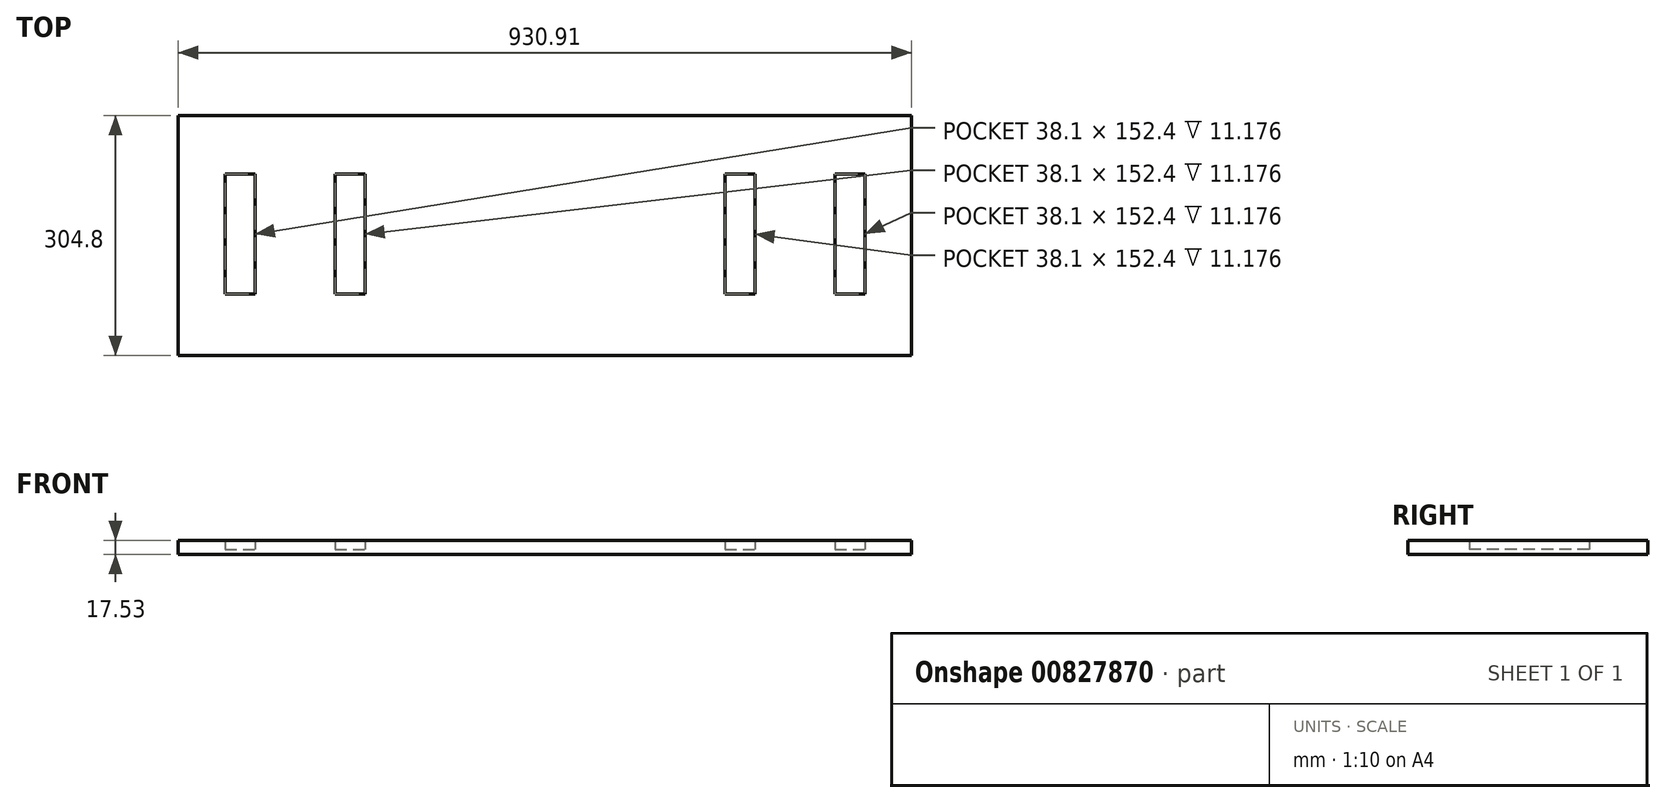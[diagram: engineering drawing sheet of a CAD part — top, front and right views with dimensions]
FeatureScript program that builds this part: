
annotation { "Feature Type Name" : "Feature", "Feature Type Description" : "" }
export const myFeature = defineFeature(function(context is Context, id is Id, definition is map)
    precondition{}
    {
        {
            var Q0;
            Q0=qCreatedBy(makeId("Top.planeOp"),FACE);
            var sketch = newSketch(context, id + "F0", { "sketchPlane" : qUnion([Q0])});
            skLineSegment(sketch, "E0.bottom", {"start": v(-457.2, 150.48) * mm, "end": v(457.2, 150.48) * mm});
            skLineSegment(sketch, "E0.top", {"start": v(-457.2, -154.32) * mm, "end": v(457.2, -154.32) * mm});
            skLineSegment(sketch, "E0.left", {"start": v(-457.2, 150.48) * mm, "end": v(-457.2, -154.32) * mm});
            skLineSegment(sketch, "E0.right", {"start": v(457.2, 150.48) * mm, "end": v(457.2, -154.32) * mm});
            skPoint(sketch, "E0.middle", {"position": v(0, -1.92) * mm});
            skLineSegment(sketch, "E1", {"start": v(0, 0) * mm, "end": v(-457.2, 0) * mm, "construction": true});
            skLineSegment(sketch, "E2", {"start": v(0, 0) * mm, "end": v(457.2, 0) * mm, "construction": true});
            skLineSegment(sketch, "E3.bottom", {"start": v(-406.4, 76.2) * mm, "end": v(-368.3, 76.2) * mm});
            skLineSegment(sketch, "E3.top", {"start": v(-406.4, -76.2) * mm, "end": v(-368.3, -76.2) * mm});
            skLineSegment(sketch, "E3.left", {"start": v(-406.4, 76.2) * mm, "end": v(-406.4, -76.2) * mm});
            skLineSegment(sketch, "E3.right", {"start": v(-368.3, 76.2) * mm, "end": v(-368.3, -76.2) * mm});
            skPoint(sketch, "E3.middle", {"position": v(-387.35, 0) * mm});
            skLineSegment(sketch, "E4.bottom", {"start": v(-266.7, 76.2) * mm, "end": v(-228.6, 76.2) * mm});
            skLineSegment(sketch, "E4.top", {"start": v(-266.7, -76.2) * mm, "end": v(-228.6, -76.2) * mm});
            skLineSegment(sketch, "E4.left", {"start": v(-266.7, 76.2) * mm, "end": v(-266.7, -76.2) * mm});
            skLineSegment(sketch, "E4.right", {"start": v(-228.6, 76.2) * mm, "end": v(-228.6, -76.2) * mm});
            skPoint(sketch, "E4.middle", {"position": v(-247.65, 0) * mm});
            skLineSegment(sketch, "E5.bottom", {"start": v(368.3, 76.2) * mm, "end": v(406.4, 76.2) * mm});
            skLineSegment(sketch, "E5.top", {"start": v(368.3, -76.2) * mm, "end": v(406.4, -76.2) * mm});
            skLineSegment(sketch, "E5.left", {"start": v(368.3, 76.2) * mm, "end": v(368.3, -76.2) * mm});
            skLineSegment(sketch, "E5.right", {"start": v(406.4, 76.2) * mm, "end": v(406.4, -76.2) * mm});
            skPoint(sketch, "E5.middle", {"position": v(387.35, 0) * mm});
            skLineSegment(sketch, "E6.bottom", {"start": v(228.6, 76.2) * mm, "end": v(266.7, 76.2) * mm});
            skLineSegment(sketch, "E6.top", {"start": v(228.6, -76.2) * mm, "end": v(266.7, -76.2) * mm});
            skLineSegment(sketch, "E6.left", {"start": v(228.6, 76.2) * mm, "end": v(228.6, -76.2) * mm});
            skLineSegment(sketch, "E6.right", {"start": v(266.7, 76.2) * mm, "end": v(266.7, -76.2) * mm});
            skPoint(sketch, "E6.middle", {"position": v(247.65, 0) * mm});
            skLineSegment(sketch, "E7", {"start": v(266.7, 43.43) * mm, "end": v(368.3, 43.43) * mm, "construction": true});
            skLineSegment(sketch, "E8", {"start": v(-368.3, 33.3) * mm, "end": v(-266.7, 33.3) * mm, "construction": true});
            skLineSegment(sketch, "E9", {"start": v(-406.4, 21.9) * mm, "end": v(-457.2, 21.9) * mm, "construction": true});
            skLineSegment(sketch, "E10", {"start": v(406.4, 33.3) * mm, "end": v(457.2, 33.3) * mm, "construction": true});
            skLineSegment(sketch, "E11", {"start": v(-457.2, 150.48) * mm, "end": v(-465.46, 150.48) * mm});
            skLineSegment(sketch, "E12", {"start": v(-465.46, 150.48) * mm, "end": v(-465.46, -154.32) * mm});
            skLineSegment(sketch, "E13", {"start": v(-465.46, -154.32) * mm, "end": v(-457.2, -154.32) * mm});
            skLineSegment(sketch, "E14", {"start": v(457.2, 150.48) * mm, "end": v(465.45, 150.48) * mm});
            skLineSegment(sketch, "E15", {"start": v(465.45, 150.48) * mm, "end": v(465.45, -154.32) * mm});
            skLineSegment(sketch, "E16", {"start": v(465.45, -154.32) * mm, "end": v(457.2, -154.32) * mm});
            skSolve(sketch);
        }
        {
            var Q0;
            Q0 = qSketchRegion(id + "F0", true);
            extrude(context, id + "F1", {"entities" : qUnion([Q0]), "depth" : 17.53 * mm, "offsetDistance" : 25.4 * mm});
        }
        {
            var Q0;
            Q0=makeQuery(id+"F0.imprint","IMPRINT",FACE,{"disambiguationData":[TD([[makeQuery(id+"F0.imprint","IMPRINT",EDGE,{"derivedFrom":sQuery(id+"F0.wireOp",EDGE,"E3.bottom")}),-1.0]])]});
            var Q1;
            Q1=makeQuery(id+"F0.imprint","IMPRINT",FACE,{"disambiguationData":[TD([[makeQuery(id+"F0.imprint","IMPRINT",EDGE,{"derivedFrom":sQuery(id+"F0.wireOp",EDGE,"E4.bottom")}),-1.0]])]});
            var Q2;
            Q2=makeQuery(id+"F0.imprint","IMPRINT",FACE,{"disambiguationData":[TD([[makeQuery(id+"F0.imprint","IMPRINT",EDGE,{"derivedFrom":sQuery(id+"F0.wireOp",EDGE,"E6.bottom")}),-1.0]])]});
            var Q3;
            Q3=makeQuery(id+"F0.imprint","IMPRINT",FACE,{"disambiguationData":[TD([[makeQuery(id+"F0.imprint","IMPRINT",EDGE,{"derivedFrom":sQuery(id+"F0.wireOp",EDGE,"E5.bottom")}),-1.0]])]});
            extrude(context, id + "F2", {"entities" : qUnion([Q0, Q1, Q2, Q3]), "operationType" : NewBodyOperationType.ADD, "depth" : 6.35 * mm, "offsetDistance" : 25.4 * mm});
        }
    });
